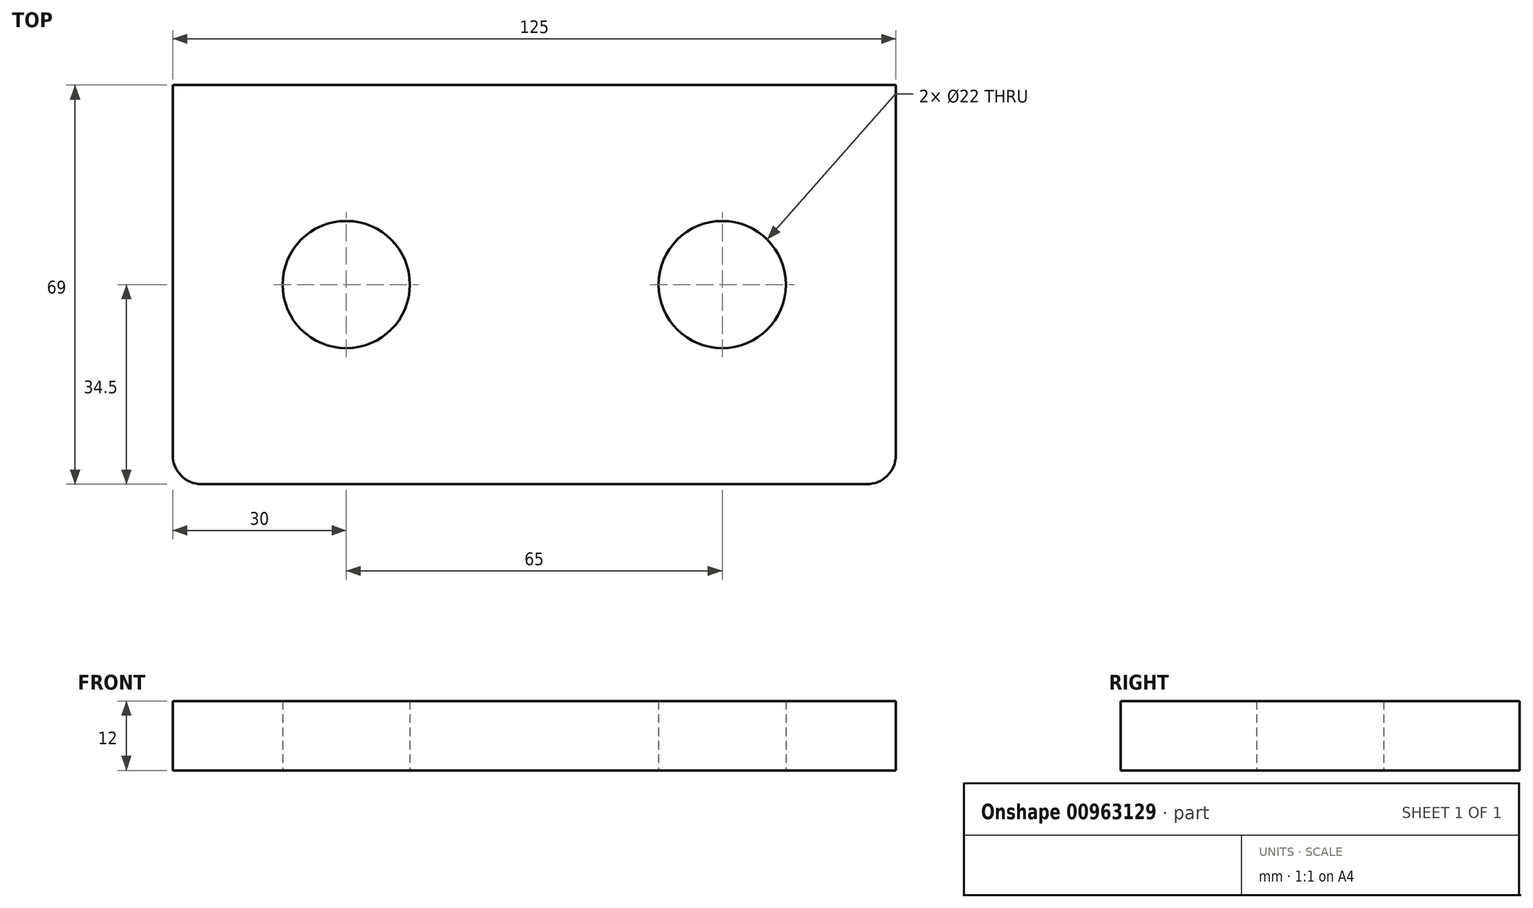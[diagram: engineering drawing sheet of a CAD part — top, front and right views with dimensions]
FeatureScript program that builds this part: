
annotation { "Feature Type Name" : "Feature", "Feature Type Description" : "" }
export const myFeature = defineFeature(function(context is Context, id is Id, definition is map)
    precondition{}
    {
        {
            var Q0;
            Q0=qCreatedBy(makeId("Top.planeOp"),FACE);
            var sketch = newSketch(context, id + "F0", { "sketchPlane" : qUnion([Q0])});
            skLineSegment(sketch, "E0.bottom", {"start": v(-57.5, -34.5) * mm, "end": v(57.5, -34.5) * mm});
            skLineSegment(sketch, "E0.top", {"start": v(-62.5, 34.5) * mm, "end": v(62.5, 34.5) * mm});
            skLineSegment(sketch, "E0.left", {"start": v(-62.5, -29.5) * mm, "end": v(-62.5, 34.5) * mm});
            skLineSegment(sketch, "E0.right", {"start": v(62.5, -29.5) * mm, "end": v(62.5, 34.5) * mm});
            skPoint(sketch, "E0.middle", {"position": v(0, 0) * mm});
            skCircle(sketch, "E1", {"center": v(-32.5, 0) * mm, "radius": 11 * mm});
            skCircle(sketch, "E2", {"center": v(32.5, 0) * mm, "radius": 11 * mm});
            skPoint(sketch, "E3.visualSharp", {"position": v(-62.5, -34.5) * mm});
            skArc(sketch, "E3.filletArc", {"start": v(-62.5, -29.5) * mm, "mid": v(-61.04, -33.04) * mm, "end": v(-57.5, -34.5) * mm});
            skPoint(sketch, "E4.visualSharp", {"position": v(62.5, -34.5) * mm});
            skArc(sketch, "E4.filletArc", {"start": v(57.5, -34.5) * mm, "mid": v(61.04, -33.04) * mm, "end": v(62.5, -29.5) * mm});
            skSolve(sketch);
        }
        {
            var Q0;
            Q0=makeQuery(id+"F0.imprint","IMPRINT",FACE,{"disambiguationData":[TD([[makeQuery(id+"F0.imprint","IMPRINT",EDGE,{"derivedFrom":sQuery(id+"F0.wireOp",EDGE,"E0.bottom")}),1.0]])]});
            extrude(context, id + "F1", {"entities" : qUnion([Q0]), "depth" : 12 * mm, "offsetDistance" : 25 * mm});
        }
    });
